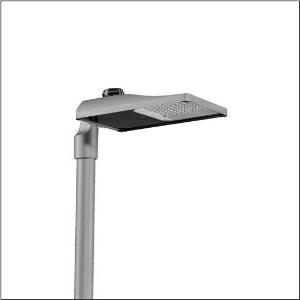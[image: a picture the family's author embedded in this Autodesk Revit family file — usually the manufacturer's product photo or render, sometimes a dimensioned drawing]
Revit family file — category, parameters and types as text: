
# Revit family: streetlight_sl_31_midi___st0_5a_5xh7b75n08na_00dd
name_source: partatom
category: Lighting Fixtures
units: mm (PartAtom-declared; Revit-internal decimal feet)

## family parameters
Cut with Voids When Loaded = No
Host = Face
Light Source = No
Part Type = Normal
Room Calculation Point = No
Round Connector Dimension = Use Diameter
Shared = No

## types (1)
- --- (1 x LED, 18260 lm, 149.4 W, 2200K)
    Apparent Load = 149 VA
    CIE Flux Codes = 43 76 97 100 100
    Color Rendering = 70
    Color Temperature = 2200K
    Default Elevation = 1800 mm
    Description = Streetlight SL 31 midi NEMA (7pin), Desk-Remote mast luminaire for post-top, side-entry; light control with lens of PMMA; light distribution: ST0.5a, direct asymmetric distribution, for standard-compliant lighting for roads and squares; LED: luminous flux: 18.260lm, light colour: 722, colour temperature: 2200K; luminous efficacy: 122,2lm/W; control: pre-setting: linear dimming characteristic, flexible luminous flux parameterisation, time-dependent luminous flux control, constant luminous flux control, intelligent temperature release in ECG and LED module, overheat protection; luminaire housing, of diecast aluminium, SITECO metallic grey (DB 702S), corrosivity category C5 high according to DIN EN ISO 12944; cover of toughened safety glass, transparent, opened without tools; mast flange of diecast aluminium, SITECO metallic grey (DB 702S), spigot size: 76/60mm, mast flange included unmounted; cable length: 12,5m, connection cable pre-assembled; mains connection: 220..240V, AC, 50/60Hz; power consumption (at start of service life): 149,4W / (at end of service life): 163,4W / (with reduced operation 50%): 66,1W; protection rating (complete): IP66; insulation class (complete): insulation class I (protective earthing); impact resistance: IK10; certification: CE, ENEC, ENEC+, VDE, UKCA; permissible operating ambient temperature for outdoor applications: -40..+50°C; packaging unit: 1 piece

Light Distribution: ST0.5a
    Height = 79 mm
    Lamp = 1 x LED
    Lamp Light Flux = 18260 lm
    Lamp Power = 149.4 W
    Lamp count = 1
    Length = 577 mm
    Luminous efficacy = 122 lm/W
    Manufacturer = Siteco
    ModVariant = No
    Model = 5XH7B75N08NA
    Number of Poles = 1
    OnlyDefault = Yes
    Power Factor = 1
    Product Name = Streetlight SL 31 midi | ST0.5a
    Product group = mast luminaire | pylon top
    ProductGroupID = 6100
    Protection Class = Protection class I
    Protection Degree = IP 66
    RLX_Detail_Level = 1
    RLX_Emergency_Light_Flux = 0 lm
    RLX_Emergency_Type = 0
    RLX_Emergency_Type_DB = No
    RlxData = <blob elided: 37601 chars, md5=3fd793b4>
    Socket = socket
    Standby Power = 0 W
    System Light Flux = 18260 lm
    System Power = 149 W
    Type Comments = factory setting: luminous flux: 100 % | dim-lin: 254 | 796 mA
    Type Image = l_1300282.jpg
    URL = http://relux.com
    VarID = @adj_009661
    Voltage = 0 V
    Weight = 0.00 kg
    Width = 362 mm

## geometry (parser evidence)
native form markers: Blend x4, Sweep x11
no freeform markers — native parametric forms only
